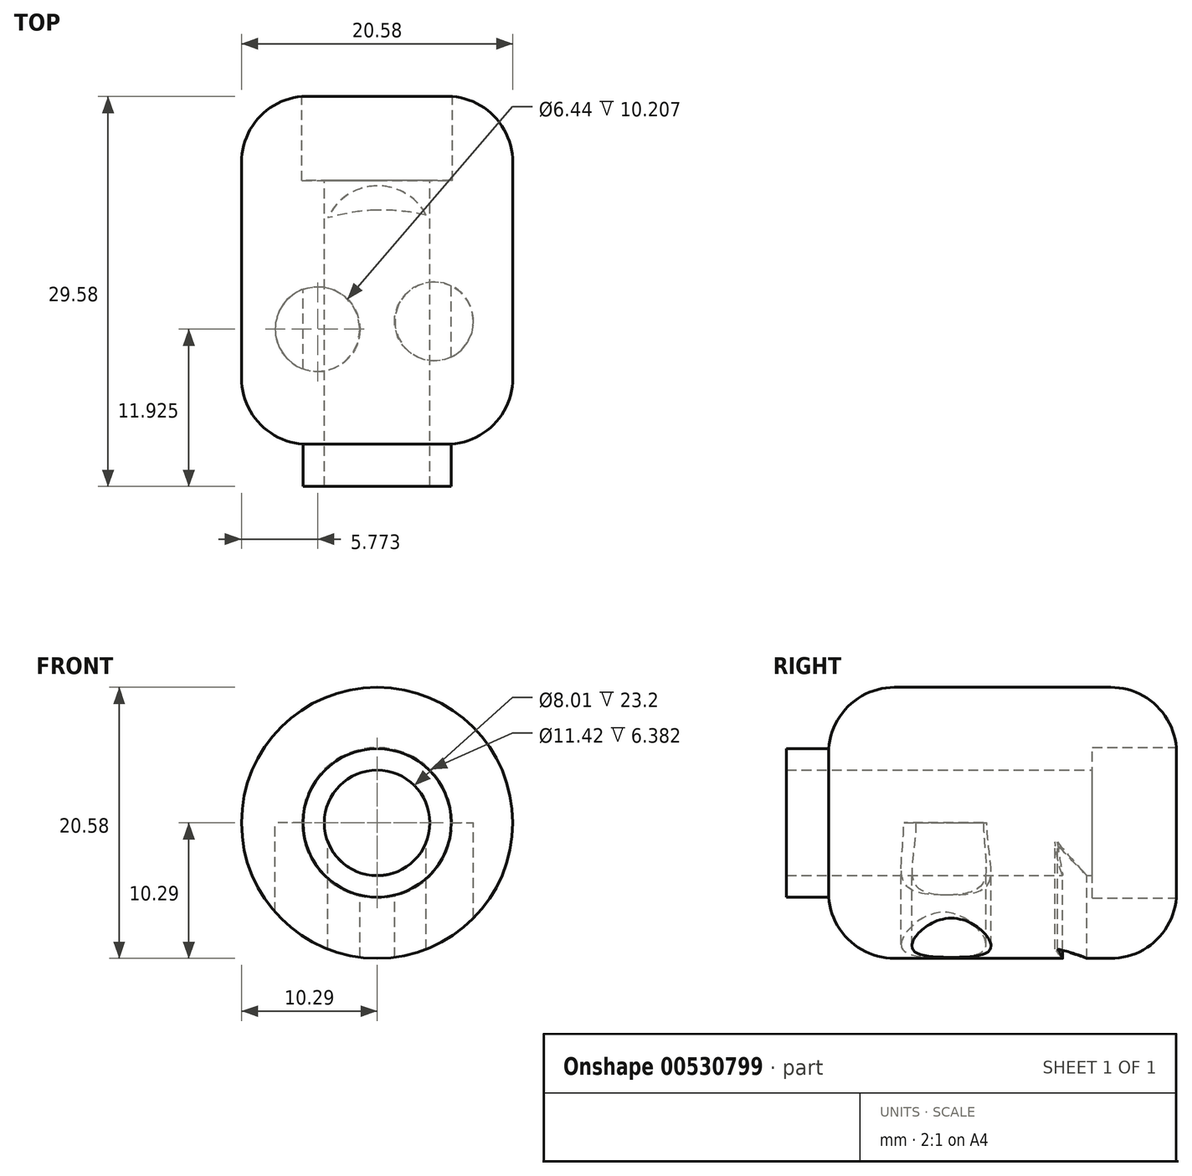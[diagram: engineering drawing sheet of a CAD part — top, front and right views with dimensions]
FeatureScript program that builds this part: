
annotation { "Feature Type Name" : "Feature", "Feature Type Description" : "" }
export const myFeature = defineFeature(function(context is Context, id is Id, definition is map)
    precondition{}
    {
        {
            var Q0;
            Q0=qCreatedBy(makeId("Front.planeOp"),FACE);
            var sketch = newSketch(context, id + "F0", { "sketchPlane" : qUnion([Q0])});
            skCircle(sketch, "E0", {"center": v(0, 0) * mm, "radius": 10.29 * mm});
            skSolve(sketch);
        }
        {
            var Q0;
            Q0=qCreatedBy(makeId("Front.planeOp"),FACE);
            var sketch = newSketch(context, id + "F1", { "sketchPlane" : qUnion([Q0])});
            skSolve(sketch);
        }
        {
            var Q0;
            Q0 = qSketchRegion(id + "F1", true);
            var Q1;
            Q1=makeQuery(id+"F0.imprint","IMPRINT",FACE,{"disambiguationData":[TD([[makeQuery(id+"F0.imprint","IMPRINT",EDGE,{"derivedFrom":sQuery(id+"F0.wireOp",EDGE,"E0")}),1.0]])]});
            extrude(context, id + "F2", {"entities" : qUnion([Q0, Q1]), "depth" : 26.4 * mm, "offsetDistance" : 25 * mm});
        }
        {
            var Q0;
            Q0=qCreatedBy(makeId("Front.planeOp"),FACE);
            var sketch = newSketch(context, id + "F3", { "sketchPlane" : qUnion([Q0])});
            skCircle(sketch, "E1", {"center": v(0, 0) * mm, "radius": 5.48 * mm});
            skSolve(sketch);
        }
        {
            var Q0;
            Q0=makeQuery(id+"F2.opExtrude","CAP_EDGE",EDGE,{"disambiguationData":[OSD([sQuery(id+"F0.wireOp",EDGE,"E0")])],"isStart":false});
            var Q1;
            Q1=makeQuery(id+"F2.opExtrude","CAP_EDGE",EDGE,{"disambiguationData":[OSD([sQuery(id+"F0.wireOp",EDGE,"E0")])],"isStart":true});
            fillet(context, id + "F4", {"entities" : qUnion([Q0, Q1]), "radius" : 5 * mm, "tangentPropagation" : true, "allowEdgeOverflow" : false});
        }
        {
            var Q0;
            Q0=qCreatedBy(makeId("Front.planeOp"),FACE);
            var sketch = newSketch(context, id + "F5", { "sketchPlane" : qUnion([Q0])});
            skCircle(sketch, "E2", {"center": v(0, 0) * mm, "radius": 5.46 * mm});
            skSolve(sketch);
        }
        {
            var Q0;
            Q0 = qSketchRegion(id + "F5", true);
            var Q1;
            Q1=makeQuery(id+"F3.imprint","IMPRINT",FACE,{"disambiguationData":[TD([[makeQuery(id+"F3.imprint","IMPRINT",EDGE,{"derivedFrom":sQuery(id+"F3.wireOp",EDGE,"E1")}),1.0]])]});
            extrude(context, id + "F6", {"entities" : qUnion([Q0, Q1]), "operationType" : NewBodyOperationType.REMOVE, "depth" : 10.3 * mm, "offsetDistance" : 25 * mm});
        }
        {
            var Q0;
            Q0=qCreatedBy(makeId("Top.planeOp"),FACE);
            var sketch = newSketch(context, id + "F7", { "sketchPlane" : qUnion([Q0])});
            skCircle(sketch, "E3", {"center": v(4.32, -17.09) * mm, "radius": 3 * mm});
            skSolve(sketch);
        }
        {
            var Q0;
            Q0 = qSketchRegion(id + "F7", true);
            extrude(context, id + "F8", {"entities" : qUnion([Q0]), "operationType" : NewBodyOperationType.REMOVE, "oppositeDirection" : true, "depth" : 15.6 * mm, "offsetDistance" : 25 * mm});
        }
        {
            var Q0;
            Q0=qCreatedBy(makeId("Top.planeOp"),FACE);
            var sketch = newSketch(context, id + "F9", { "sketchPlane" : qUnion([Q0])});
            skCircle(sketch, "E4", {"center": v(-4.52, -17.67) * mm, "radius": 3.22 * mm});
            skSolve(sketch);
        }
        {
            var Q0;
            Q0 = qSketchRegion(id + "F9", true);
            extrude(context, id + "F10", {"entities" : qUnion([Q0]), "operationType" : NewBodyOperationType.REMOVE, "oppositeDirection" : true, "depth" : 25 * mm, "offsetDistance" : 25 * mm});
        }
        {
            var Q0;
            Q0=qCreatedBy(makeId("Front.planeOp"),FACE);
            var sketch = newSketch(context, id + "F11", { "sketchPlane" : qUnion([Q0])});
            skCircle(sketch, "E5", {"center": v(0, 0) * mm, "radius": 5.63 * mm});
            skSolve(sketch);
        }
        {
            var Q0;
            Q0 = qSketchRegion(id + "F11", true);
            extrude(context, id + "F12", {"entities" : qUnion([Q0]), "operationType" : NewBodyOperationType.ADD, "depth" : 29.6 * mm, "offsetDistance" : 25 * mm});
        }
        {
            var Q0;
            Q0=qCreatedBy(makeId("Front.planeOp"),FACE);
            var sketch = newSketch(context, id + "F13", { "sketchPlane" : qUnion([Q0])});
            skCircle(sketch, "E6", {"center": v(0, 0) * mm, "radius": 5.7 * mm});
            skSolve(sketch);
        }
        {
            var Q0;
            Q0 = qSketchRegion(id + "F13", true);
            extrude(context, id + "F14", {"entities" : qUnion([Q0]), "operationType" : NewBodyOperationType.REMOVE, "depth" : 6.4 * mm, "offsetDistance" : 25 * mm});
        }
        {
            var Q0;
            Q0=qCreatedBy(makeId("Front.planeOp"),FACE);
            var sketch = newSketch(context, id + "F15", { "sketchPlane" : qUnion([Q0])});
            skCircle(sketch, "E7", {"center": v(0, 0) * mm, "radius": 4 * mm});
            skSolve(sketch);
        }
        {
            var Q0;
            Q0 = qSketchRegion(id + "F15", true);
            extrude(context, id + "F16", {"entities" : qUnion([Q0]), "operationType" : NewBodyOperationType.REMOVE, "endBound" : BoundingType.SYMMETRIC, "depth" : 92.2 * mm, "offsetDistance" : 25 * mm});
        }
        {
            var Q0;
            Q0=qCreatedBy(makeId("Top.planeOp"),FACE);
            var sketch = newSketch(context, id + "F17", { "sketchPlane" : qUnion([Q0])});
            skArc(sketch, "E8", {"start": v(3.73, -9.03) * mm, "mid": v(-0.06, -6.8) * mm, "end": v(-3.73, -9.23) * mm});
            skArc(sketch, "E9", {"start": v(3.73, -9.03) * mm, "mid": v(-0.01, -8.64) * mm, "end": v(-3.73, -9.23) * mm});
            skSolve(sketch);
        }
        {
            var Q0;
            Q0 = qSketchRegion(id + "F17", true);
            extrude(context, id + "F18", {"entities" : qUnion([Q0]), "operationType" : NewBodyOperationType.REMOVE, "oppositeDirection" : true, "depth" : 44.9 * mm, "offsetDistance" : 25 * mm});
        }
    });
